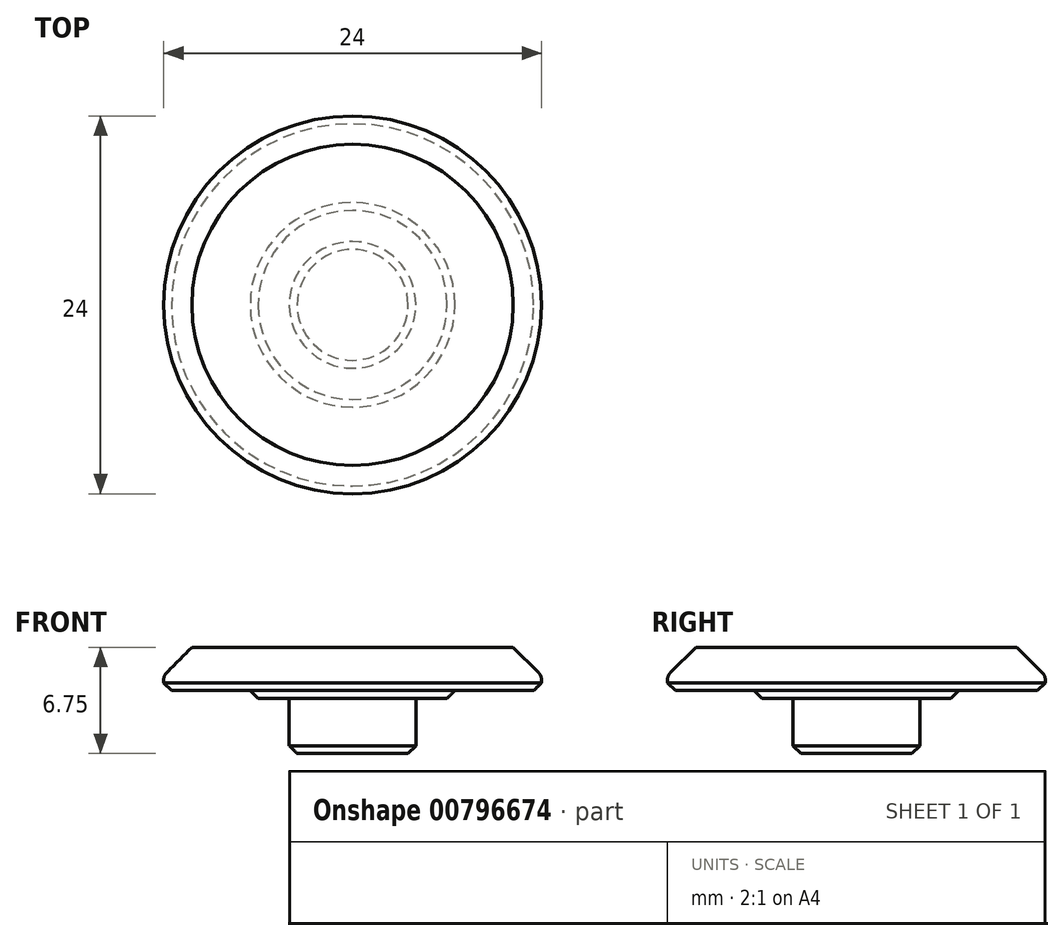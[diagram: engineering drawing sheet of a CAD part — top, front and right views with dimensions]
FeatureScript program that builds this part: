
annotation { "Feature Type Name" : "Feature", "Feature Type Description" : "" }
export const myFeature = defineFeature(function(context is Context, id is Id, definition is map)
    precondition{}
    {
        {
            var Q0;
            Q0=qCreatedBy(makeId("Top.planeOp"),FACE);
            var sketch = newSketch(context, id + "F0", { "sketchPlane" : qUnion([Q0])});
            skCircle(sketch, "E0", {"center": v(0, 0) * mm, "radius": 12 * mm});
            skSolve(sketch);
        }
        {
            var Q0;
            Q0 = qSketchRegion(id + "F0", true);
            extrude(context, id + "F1", {"entities" : qUnion([Q0]), "depth" : 2.75 * mm, "offsetDistance" : 25 * mm});
        }
        {
            var Q0;
            Q0=makeQuery(id+"F1.opExtrude","CAP_FACE",FACE,{"disambiguationData":[OSD([sQuery(id+"F0.wireOp",EDGE,"E0")])],"isStart":true});
            var sketch = newSketch(context, id + "F2", { "sketchPlane" : qUnion([Q0])});
            skCircle(sketch, "E1", {"center": v(0, 0) * mm, "radius": 4.02 * mm});
            skSolve(sketch);
        }
        {
            var Q0;
            Q0 = qSketchRegion(id + "F2", true);
            extrude(context, id + "F3", {"entities" : qUnion([Q0]), "operationType" : NewBodyOperationType.ADD, "depth" : 4 * mm, "offsetDistance" : 25 * mm});
        }
        {
            var Q0;
            Q0=makeQuery(id+"F1.opExtrude","CAP_FACE",FACE,{"disambiguationData":[OSD([sQuery(id+"F0.wireOp",EDGE,"E0")])],"isStart":true});
            var sketch = newSketch(context, id + "F4", { "sketchPlane" : qUnion([Q0])});
            skCircle(sketch, "E2", {"center": v(0, 0) * mm, "radius": 6.5 * mm});
            skSolve(sketch);
        }
        {
            var Q0;
            Q0 = qSketchRegion(id + "F4", true);
            extrude(context, id + "F5", {"entities" : qUnion([Q0]), "operationType" : NewBodyOperationType.ADD, "depth" : .5 * mm, "offsetDistance" : 25 * mm});
        }
        {
            var Q0;
            Q0=makeQuery(id+"F5.opExtrude","CAP_EDGE",EDGE,{"disambiguationData":[OSD([sQuery(id+"F4.wireOp",EDGE,"E2")])],"isStart":false});
            var Q1;
            Q1=makeQuery(id+"F3.opExtrude","CAP_EDGE",EDGE,{"disambiguationData":[OSD([sQuery(id+"F2.wireOp",EDGE,"E1")])],"isStart":false});
            var Q2;
            Q2=makeQuery(id+"F1.opExtrude","CAP_EDGE",EDGE,{"disambiguationData":[OSD([sQuery(id+"F0.wireOp",EDGE,"E0")])],"isStart":true});
            chamfer(context, id + "F6", {"entities" : qUnion([Q0, Q1, Q2]), "width" : .5 * mm, "tangentPropagation" : true});
        }
        {
            var Q0;
            Q0=makeQuery(id+"F1.opExtrude","CAP_FACE",FACE,{"disambiguationData":[OSD([sQuery(id+"F0.wireOp",EDGE,"E0")])],"isStart":false});
            chamfer(context, id + "F7", {"entities" : qUnion([Q0]), "width" : 1.8 * mm, "tangentPropagation" : true});
        }
        {
            var Q0;
            {var subQ0=sQuery(id+"F0.wireOp",EDGE,"E0");Q0=makeQuery(id+"F7.opChamfer","BLEND_EDGE",EDGE,{"blendedFrom":[makeQuery(id+"F1.opExtrude","CAP_EDGE",EDGE,{"disambiguationData":[OSD([subQ0])],"isStart":false}),makeQuery(id+"F1.opExtrude","SWEPT_FACE",FACE,{"disambiguationData":[OSD([subQ0])]})],"blendedInto":[makeQuery(id+"F1.opExtrude","SWEPT_FACE",FACE,{"disambiguationData":[OSD([subQ0])]})]});}
            fillet(context, id + "F8", {"entities" : qUnion([Q0]), "radius" : .7 * mm, "tangentPropagation" : true, "allowEdgeOverflow" : false});
        }
    });
